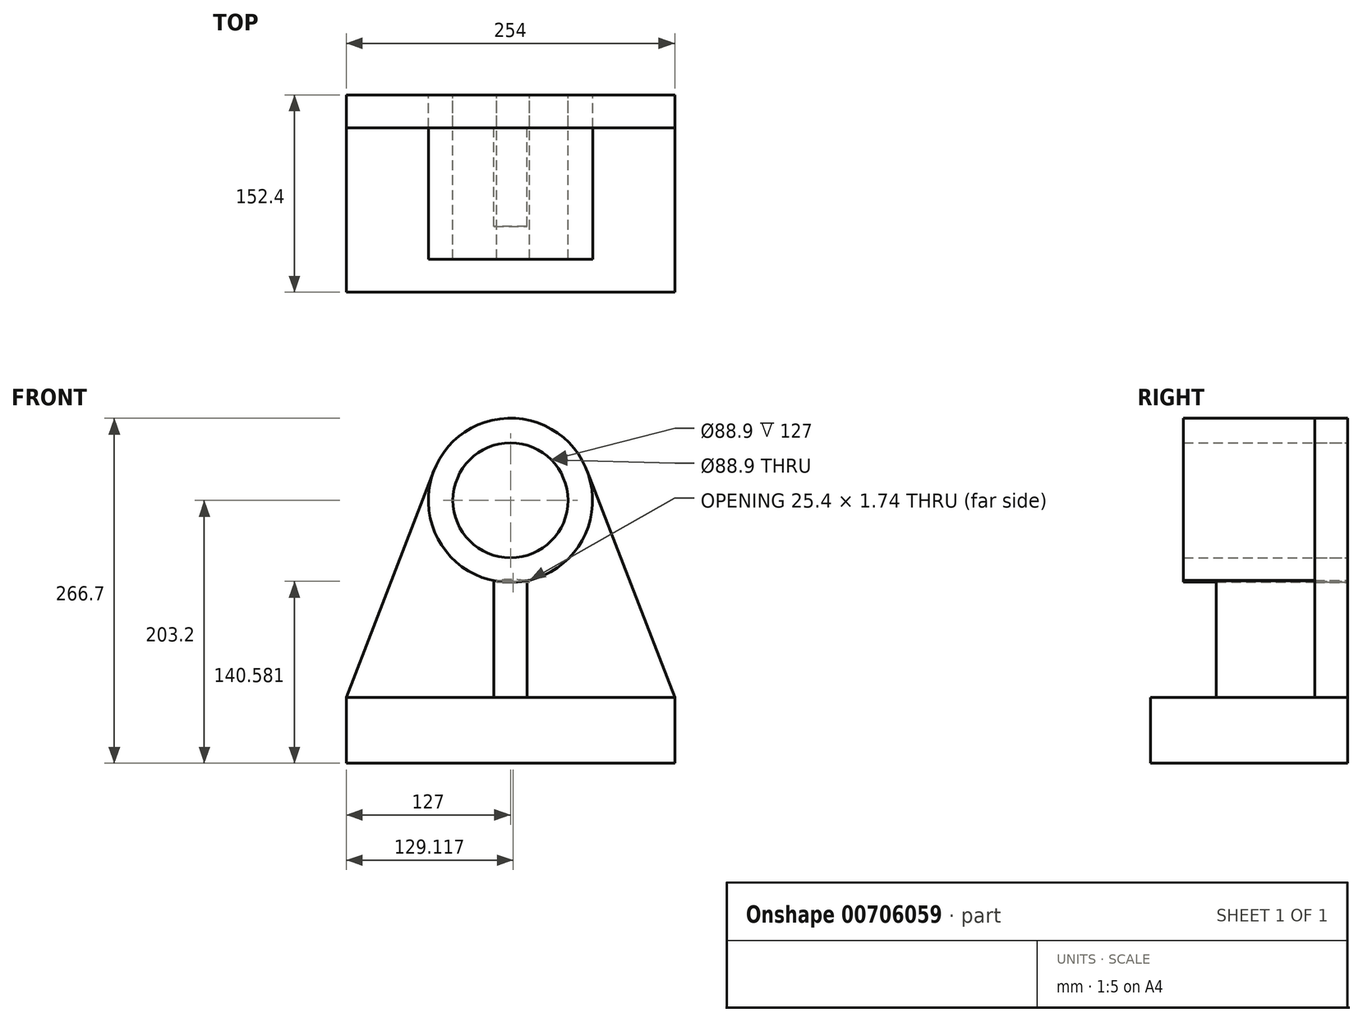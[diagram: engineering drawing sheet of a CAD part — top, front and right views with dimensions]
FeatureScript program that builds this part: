
annotation { "Feature Type Name" : "Feature", "Feature Type Description" : "" }
export const myFeature = defineFeature(function(context is Context, id is Id, definition is map)
    precondition{}
    {
        {
            var Q0;
            Q0=qCreatedBy(makeId("Front.planeOp"),FACE);
            var sketch = newSketch(context, id + "F0", { "sketchPlane" : qUnion([Q0])});
            skLineSegment(sketch, "E0.bottom", {"start": v(127, -25.4) * mm, "end": v(-127, -25.4) * mm});
            skLineSegment(sketch, "E0.top", {"start": v(127, 25.4) * mm, "end": v(-127, 25.4) * mm});
            skLineSegment(sketch, "E0.left", {"start": v(127, -25.4) * mm, "end": v(127, 25.4) * mm});
            skLineSegment(sketch, "E0.right", {"start": v(-127, -25.4) * mm, "end": v(-127, 25.4) * mm});
            skPoint(sketch, "E0.middle", {"position": v(0, 0) * mm});
            skSolve(sketch);
        }
        {
            var Q0;
            Q0 = qSketchRegion(id + "F0", true);
            extrude(context, id + "F1", {"entities" : qUnion([Q0]), "depth" : 152.4 * mm, "offsetDistance" : 25.4 * mm});
        }
        {
            var Q0;
            Q0=qCreatedBy(makeId("Front.planeOp"),FACE);
            var sketch = newSketch(context, id + "F2", { "sketchPlane" : qUnion([Q0])});
            skCircle(sketch, "E1", {"center": v(0, 177.8) * mm, "radius": 63.5 * mm});
            skCircle(sketch, "E2", {"center": v(0, 177.8) * mm, "radius": 44.45 * mm});
            skLineSegment(sketch, "E3", {"start": v(127, 25.4) * mm, "end": v(59.23, 200.7) * mm});
            skLineSegment(sketch, "E4", {"start": v(-127, 25.4) * mm, "end": v(127, 25.4) * mm});
            skLineSegment(sketch, "E5.bottom", {"start": v(-10.58, 25.4) * mm, "end": v(14.82, 25.4) * mm});
            skLineSegment(sketch, "E5.left", {"start": v(-10.58, 25.4) * mm, "end": v(-10.58, 115.19) * mm});
            skLineSegment(sketch, "E5.right", {"start": v(14.82, 25.4) * mm, "end": v(14.82, 116.05) * mm});
            skArc(sketch, "E6", {"start": v(-10.58, 115.19) * mm, "mid": v(2.16, 114.34) * mm, "end": v(14.82, 116.05) * mm});
            skArc(sketch, "E7", {"start": v(-10.58, 115.19) * mm, "mid": v(2.15, 114.55) * mm, "end": v(14.82, 116.05) * mm});
            skLineSegment(sketch, "E8", {"start": v(-127, 25.4) * mm, "end": v(-59.23, 200.7) * mm});
            skSolve(sketch);
        }
        {
            var Q0;
            Q0=makeQuery(id+"F2.imprint","IMPRINT",FACE,{"disambiguationData":[TD([[makeQuery(id+"F2.imprint","IMPRINT",EDGE,{"derivedFrom":sQuery(id+"F2.wireOp",EDGE,"E2")}),-1.0]])]});
            extrude(context, id + "F3", {"entities" : qUnion([Q0]), "depth" : 127 * mm, "offsetDistance" : 25.4 * mm});
        }
        {
            var Q0;
            Q0 = qSketchRegion(id + "F2", true);
            extrude(context, id + "F4", {"entities" : qUnion([Q0]), "depth" : 25.4 * mm, "offsetDistance" : 25.4 * mm});
        }
        {
            var Q0;
            Q0=makeQuery(id+"F4.opExtrude","CAP_FACE",FACE,{"disambiguationData":[OSD([sQuery(id+"F2.wireOp",EDGE,"E1"),sQuery(id+"F2.wireOp",EDGE,"E2"),sQuery(id+"F2.wireOp",EDGE,"E3"),sQuery(id+"F2.wireOp",EDGE,"E4"),sQuery(id+"F2.wireOp",EDGE,"E8"),sQuery(id+"F2.wireOp",EDGE,"E5.bottom")])],"isStart":false});
            var sketch = newSketch(context, id + "F5", { "sketchPlane" : qUnion([Q0])});
            skLineSegment(sketch, "E9.bottom", {"start": v(12.7, 25.4) * mm, "end": v(-12.7, 25.4) * mm});
            skLineSegment(sketch, "E9.left", {"start": v(12.7, 25.4) * mm, "end": v(12.7, 115.58) * mm});
            skLineSegment(sketch, "E9.right", {"start": v(-12.7, 25.4) * mm, "end": v(-12.7, 115.58) * mm});
            skArc(sketch, "E10", {"start": v(12.7, 115.58) * mm, "mid": v(0, 116.65) * mm, "end": v(-12.7, 115.58) * mm});
            skSolve(sketch);
        }
        {
            var Q0;
            Q0 = qSketchRegion(id + "F5", true);
            extrude(context, id + "F6", {"entities" : qUnion([Q0]), "depth" : 76.2 * mm, "offsetDistance" : 25.4 * mm});
        }
    });
